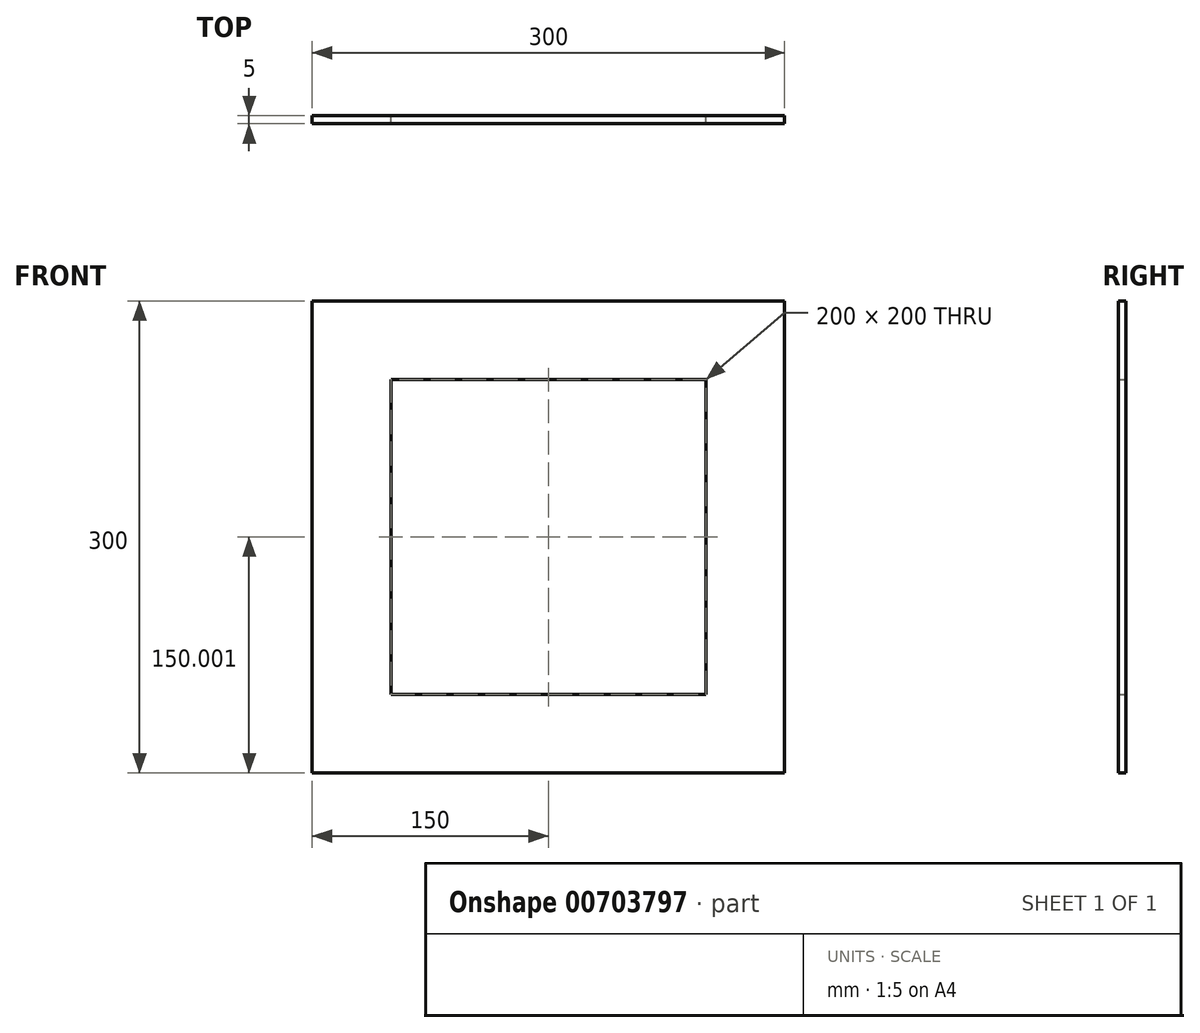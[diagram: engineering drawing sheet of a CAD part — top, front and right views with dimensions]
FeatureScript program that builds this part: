
annotation { "Feature Type Name" : "Feature", "Feature Type Description" : "" }
export const myFeature = defineFeature(function(context is Context, id is Id, definition is map)
    precondition{}
    {
        {
            var Q0;
            Q0=qCreatedBy(makeId("Front.planeOp"),FACE);
            var sketch = newSketch(context, id + "F0", { "sketchPlane" : qUnion([Q0])});
            skLineSegment(sketch, "E0", {"start": v(-71.42, 0) * mm, "end": v(71.42, 0) * mm, "construction": true});
            skLineSegment(sketch, "E1", {"start": v(0, -53.6) * mm, "end": v(0, 53.6) * mm, "construction": true});
            skLineSegment(sketch, "E2.bottom", {"start": v(-150, 162.66) * mm, "end": v(150, 162.66) * mm});
            skLineSegment(sketch, "E2.top", {"start": v(-150, -137.34) * mm, "end": v(150, -137.34) * mm});
            skLineSegment(sketch, "E2.left", {"start": v(-150, 162.66) * mm, "end": v(-150, -137.34) * mm});
            skLineSegment(sketch, "E2.right", {"start": v(150, 162.66) * mm, "end": v(150, -137.34) * mm});
            skLineSegment(sketch, "E3.bottom", {"start": v(-100, 112.66) * mm, "end": v(100, 112.66) * mm});
            skLineSegment(sketch, "E3.top", {"start": v(-100, -87.34) * mm, "end": v(100, -87.34) * mm});
            skLineSegment(sketch, "E3.left", {"start": v(-100, 112.66) * mm, "end": v(-100, -87.34) * mm});
            skLineSegment(sketch, "E3.right", {"start": v(100, 112.66) * mm, "end": v(100, -87.34) * mm});
            skSolve(sketch);
        }
        {
            var Q0;
            Q0=makeQuery(id+"F0.imprint","IMPRINT",FACE,{"disambiguationData":[TD([[makeQuery(id+"F0.imprint","IMPRINT",EDGE,{"derivedFrom":sQuery(id+"F0.wireOp",EDGE,"E2.bottom")}),-1.0]])]});
            extrude(context, id + "F1", {"entities" : qUnion([Q0]), "depth" : 5 * mm, "offsetDistance" : 25 * mm});
        }
    });
